FCSTD DOCUMENT  (FreeCAD 0.16R6706 (Git))
Label: Leiste_kurz_mitAufnahme_5x
License: All rights reserved
LicenseURL: http://de.wikipedia.org/wiki/Alle_Rechte_vorbehalten
objects: Sketcher::SketchObject×1
note: 1 computed .brp shape members not serialized (recipe doc carries the construction recipe); baked Part::Feature solids carry a one-line shape summary decoded from their .brp

FEATURE [Sketcher::SketchObject] Sketch
  sketch-geometry (60):
    g0: LineSegment StartX=0 StartY=0 StartZ=0 EndX=0 EndY=17 EndZ=0
    g1: LineSegment StartX=0 StartY=17 StartZ=0 EndX=23 EndY=17 EndZ=0
    g2: LineSegment StartX=31.5 StartY=15 StartZ=0 EndX=31.5 EndY=8.5 EndZ=0
    g3: LineSegment StartX=31.5 StartY=8.5 StartZ=0 EndX=34.5 EndY=8.5 EndZ=0
    g4: LineSegment StartX=34.5 StartY=8.5 StartZ=0 EndX=34.5 EndY=15 EndZ=0
    g5: LineSegment StartX=43 StartY=17 StartZ=0 EndX=59.5 EndY=17 EndZ=0
    g6: LineSegment StartX=59.5 StartY=17 StartZ=0 EndX=59.5 EndY=8.5 EndZ=0
    g7: LineSegment StartX=59.5 StartY=8.5 StartZ=0 EndX=62.5 EndY=8.5 EndZ=0
    g8: LineSegment StartX=62.5 StartY=8.5 StartZ=0 EndX=62.5 EndY=17 EndZ=0
    g9: LineSegment StartX=62.5 StartY=17 StartZ=0 EndX=87.5 EndY=17 EndZ=0
    g10: LineSegment StartX=87.5 StartY=17 StartZ=0 EndX=87.5 EndY=8.5 EndZ=0
    g11: LineSegment StartX=87.5 StartY=8.5 StartZ=0 EndX=90.5 EndY=8.5 EndZ=0
    g12: LineSegment StartX=90.5 StartY=8.5 StartZ=0 EndX=90.5 EndY=17 EndZ=0
    g13: LineSegment StartX=90.5 StartY=17 StartZ=0 EndX=115.5 EndY=17 EndZ=0
    g14: LineSegment StartX=115.5 StartY=17 StartZ=0 EndX=115.5 EndY=8.5 EndZ=0
    g15: LineSegment StartX=115.5 StartY=8.5 StartZ=0 EndX=118.5 EndY=8.5 EndZ=0
    g16: LineSegment StartX=118.5 StartY=8.5 StartZ=0 EndX=118.5 EndY=17 EndZ=0
    g17: LineSegment StartX=118.5 StartY=17 StartZ=0 EndX=143.5 EndY=17 EndZ=0
    g18: LineSegment StartX=143.5 StartY=17 StartZ=0 EndX=143.5 EndY=8.5 EndZ=0
    g19: LineSegment StartX=143.5 StartY=8.5 StartZ=0 EndX=146.5 EndY=8.5 EndZ=0
    g20: LineSegment StartX=146.5 StartY=8.5 StartZ=0 EndX=146.5 EndY=17 EndZ=0
    g21: LineSegment StartX=146.5 StartY=17 StartZ=0 EndX=171.5 EndY=17 EndZ=0
    g22: LineSegment StartX=171.5 StartY=17 StartZ=0 EndX=171.5 EndY=8.5 EndZ=0
    g23: LineSegment StartX=171.5 StartY=8.5 StartZ=0 EndX=174.5 EndY=8.5 EndZ=0
    g24: LineSegment StartX=174.5 StartY=8.5 StartZ=0 EndX=174.5 EndY=17 EndZ=0
    g25: LineSegment StartX=174.5 StartY=17 StartZ=0 EndX=199.5 EndY=17 EndZ=0
    g26: LineSegment StartX=199.5 StartY=17 StartZ=0 EndX=199.5 EndY=8.5 EndZ=0
    g27: LineSegment StartX=199.5 StartY=8.5 StartZ=0 EndX=202.5 EndY=8.5 EndZ=0
    g28: LineSegment StartX=202.5 StartY=8.5 StartZ=0 EndX=202.5 EndY=17 EndZ=0
    g29: LineSegment StartX=202.5 StartY=17 StartZ=0 EndX=227.5 EndY=17 EndZ=0
    g30: LineSegment StartX=227.5 StartY=17 StartZ=0 EndX=227.5 EndY=8.5 EndZ=0
    g31: LineSegment StartX=227.5 StartY=8.5 StartZ=0 EndX=230.5 EndY=8.5 EndZ=0
    g32: LineSegment StartX=230.5 StartY=8.5 StartZ=0 EndX=230.5 EndY=17 EndZ=0
    g33: LineSegment StartX=255.5 StartY=15 StartZ=0 EndX=255.5 EndY=8.5 EndZ=0
    g34: LineSegment StartX=255.5 StartY=8.5 StartZ=0 EndX=258.5 EndY=8.5 EndZ=0
    g35: LineSegment StartX=258.5 StartY=8.5 StartZ=0 EndX=258.5 EndY=15 EndZ=0
    g36: LineSegment StartX=283.5 StartY=17 StartZ=0 EndX=283.5 EndY=8.5 EndZ=0
    g37: LineSegment StartX=283.5 StartY=8.5 StartZ=0 EndX=286.5 EndY=8.5 EndZ=0
    g38: LineSegment StartX=286.5 StartY=8.5 StartZ=0 EndX=286.5 EndY=17 EndZ=0
    g39: LineSegment StartX=286.5 StartY=17 StartZ=0 EndX=311.5 EndY=17 EndZ=0
    g40: LineSegment StartX=311.5 StartY=17 StartZ=0 EndX=311.5 EndY=8.5 EndZ=0
    g41: LineSegment StartX=311.5 StartY=8.5 StartZ=0 EndX=314.5 EndY=8.5 EndZ=0
    g42: LineSegment StartX=314.5 StartY=8.5 StartZ=0 EndX=314.5 EndY=17 EndZ=0
    g43: LineSegment StartX=314.5 StartY=17 StartZ=0 EndX=345.5 EndY=17 EndZ=0
    g44: LineSegment StartX=345.5 StartY=17 StartZ=0 EndX=345.5 EndY=0 EndZ=0
    g45: LineSegment StartX=345.5 StartY=0 StartZ=0 EndX=0 EndY=0 EndZ=0
    g46: LineSegment StartX=23 StartY=17 StartZ=0 EndX=23 EndY=15 EndZ=0
    g47: LineSegment StartX=43 StartY=15 StartZ=0 EndX=43 EndY=17 EndZ=0
    g48: LineSegment StartX=23 StartY=15 StartZ=0 EndX=31.5 EndY=15 EndZ=0
    g49: LineSegment StartX=34.5 StartY=15 StartZ=0 EndX=43 EndY=15 EndZ=0
    g50: LineSegment [constr] StartX=23 StartY=17 StartZ=0 EndX=43 EndY=17 EndZ=0
    g51: LineSegment [constr] StartX=33 StartY=8.5 StartZ=0 EndX=33 EndY=17 EndZ=0
    g52: LineSegment StartX=267 StartY=17 StartZ=0 EndX=267 EndY=15 EndZ=0
    g53: LineSegment StartX=247 StartY=15 StartZ=0 EndX=247 EndY=17 EndZ=0
    g54: LineSegment StartX=247 StartY=15 StartZ=0 EndX=255.5 EndY=15 EndZ=0
    g55: LineSegment StartX=258.5 StartY=15 StartZ=0 EndX=267 EndY=15 EndZ=0
    g56: LineSegment [constr] StartX=247 StartY=17 StartZ=0 EndX=267 EndY=17 EndZ=0
    g57: LineSegment [constr] StartX=257 StartY=17 StartZ=0 EndX=257 EndY=8.5 EndZ=0
    g58: LineSegment StartX=230.5 StartY=17 StartZ=0 EndX=247 EndY=17 EndZ=0
    g59: LineSegment StartX=267 StartY=17 StartZ=0 EndX=283.5 EndY=17 EndZ=0
  constraints (176):
    c: Coincident(g-1,g0)
    c: PointOnObject(g0,g-2)
    c: Coincident(g0,g1)
    c: Horizontal(g1)
    c: Vertical(g2)
    c: Coincident(g2,g3)
    c: Horizontal(g3)
    c: Coincident(g3,g4)
    c: Vertical(g4)
    c: Horizontal(g5)
    c: DistanceX(g2,g3) = 3
    c: Equal(g2,g4)
    c: Coincident(g5,g6)
    c: Vertical(g6)
    c: Coincident(g6,g7)
    c: Horizontal(g7)
    c: Coincident(g7,g8)
    c: Vertical(g8)
    c: Coincident(g8,g9)
    c: Horizontal(g9)
    c: Coincident(g9,g10)
    c: Vertical(g10)
    c: Coincident(g10,g11)
    c: Horizontal(g11)
    c: Coincident(g11,g12)
    c: Vertical(g12)
    c: Coincident(g12,g13)
    c: Horizontal(g13)
    c: Coincident(g13,g14)
    c: Vertical(g14)
    c: Coincident(g14,g15)
    c: Horizontal(g15)
    c: Coincident(g15,g16)
    c: Vertical(g16)
    c: Coincident(g16,g17)
    c: Horizontal(g17)
    c: Coincident(g17,g18)
    c: Vertical(g18)
    c: Coincident(g18,g19)
    c: Horizontal(g19)
    c: Coincident(g19,g20)
    c: Vertical(g20)
    c: Coincident(g20,g21)
    c: Horizontal(g21)
    c: Coincident(g21,g22)
    c: Vertical(g22)
    c: Coincident(g22,g23)
    c: Horizontal(g23)
    c: Coincident(g23,g24)
    c: Vertical(g24)
    c: Coincident(g24,g25)
    c: Horizontal(g25)
    c: Coincident(g25,g26)
    c: Vertical(g26)
    c: Coincident(g26,g27)
    c: Horizontal(g27)
    c: Coincident(g27,g28)
    c: Vertical(g28)
    c: Coincident(g28,g29)
    c: Horizontal(g29)
    c: Coincident(g29,g30)
    c: Vertical(g30)
    c: Coincident(g30,g31)
    c: Horizontal(g31)
    c: Coincident(g31,g32)
    c: Vertical(g32)
    c: Vertical(g33)
    c: Coincident(g33,g34)
    c: Horizontal(g34)
    c: Coincident(g34,g35)
    c: Vertical(g35)
    c: Vertical(g36)
    c: Coincident(g36,g37)
    c: Horizontal(g37)
    c: Coincident(g37,g38)
    c: Vertical(g38)
    c: Coincident(g38,g39)
    c: Horizontal(g39)
    c: Coincident(g39,g40)
    c: Vertical(g40)
    c: Coincident(g40,g41)
    c: Horizontal(g41)
    c: Coincident(g41,g42)
    c: Vertical(g42)
    c: Horizontal(g43)
    c: Coincident(g43,g44)
    c: Vertical(g44)
    c: Equal(g8,g10)
    c: Equal(g10,g12)
    c: Equal(g12,g14)
    c: Equal(g14,g16)
    c: Equal(g16,g18)
    c: Equal(g18,g20)
    c: Equal(g20,g22)
    c: Equal(g22,g24)
    c: Equal(g24,g26)
    c: Equal(g26,g28)
    c: Equal(g28,g30)
    c: Equal(g30,g32)
    c: Equal(g36,g38)
    c: Equal(g38,g40)
    c: Equal(g40,g42)
    c: Equal(g9,g13)
    c: Equal(g3,g7)
    c: Equal(g7,g11)
    c: DistanceX(g-1,g44) = 345.5
    c: Equal(g13,g17)
    c: Equal(g17,g21)
    c: Equal(g11,g15)
    c: Equal(g15,g19)
    c: Equal(g21,g25)
    c: Equal(g25,g29)
    c: Equal(g19,g23)
    c: Equal(g23,g27)
    c: Equal(g27,g31)
    c: Equal(g31,g34)
    c: Equal(g34,g37)
    c: Equal(g37,g41)
    c: DistanceY(g-1,g0) = 17
    c: Coincident(g42,g43)
    c: Vertical(g46)
    c: Vertical(g47)
    c: Coincident(g48,g46)
    c: Horizontal(g48)
    c: Horizontal(g49)
    c: Coincident(g49,g47)
    c: Coincident(g4,g49)
    c: Coincident(g2,g48)
    c: Coincident(g1,g46)
    c: Coincident(g5,g47)
    c: Equal(g46,g47)
    c: Coincident(g50,g1)
    c: Coincident(g50,g5)
    c: PointOnObject(g51,g3)
    c: PointOnObject(g51,g50)
    c: DistanceY(g2,g1) = 8.5
    c: DistanceY(g47,g5) = 2
    c: DistanceX(g1,g5) = 20
    c: Symmetric(g1,g5,g51)
    c: Symmetric(g2,g4,g51)
    c: Equal(g6,g51)
    c: DistanceX(g0,g2) = 31.5
    c: Coincident(g-1,g45)
    c: DistanceX(g2,g5) = 28
    c: DistanceX(g5,g9) = 28
    c: Equal(g6,g8)
    c: Vertical(g52)
    c: Vertical(g53)
    c: Coincident(g54,g53)
    c: Coincident(g55,g52)
    c: Horizontal(g54)
    c: Coincident(g54,g33)
    c: Coincident(g55,g35)
    c: Tangent(g54,g55)
    c: Horizontal(g56)
    c: PointOnObject(g57,g56)
    c: PointOnObject(g57,g34)
    c: Symmetric(g33,g35,g57)
    c: Symmetric(g53,g52,g57)
    c: Equal(g56,g50)
    c: Equal(g57,g51)
    c: Coincident(g45,g44)
    c: Equal(g29,g39)
    c: Equal(g52,g47)
    c: Horizontal(g45)
    c: Coincident(g56,g53)
    c: Coincident(g56,g52)
    c: Coincident(g58,g32)
    c: Coincident(g58,g53)
    c: Horizontal(g58)
    c: Coincident(g59,g52)
    c: Coincident(g59,g36)
    c: Horizontal(g59)
    c: DistanceX(g29,g33) = 28
    c: DistanceX(g33,g36) = 28
    c: Equal(g32,g36)
